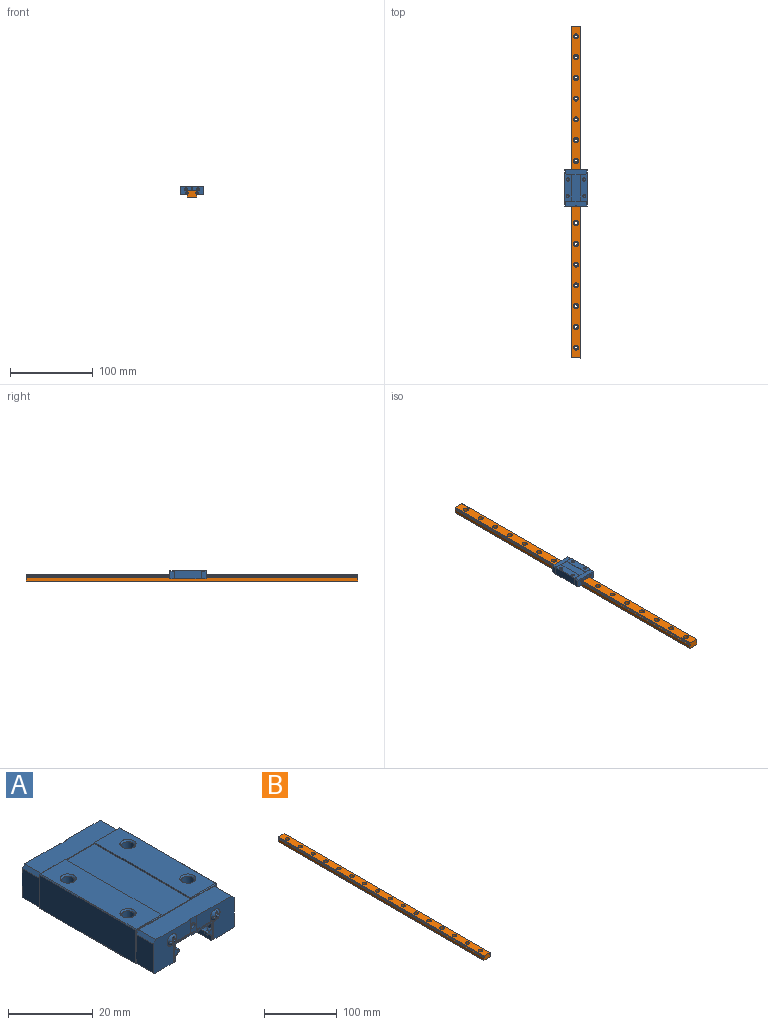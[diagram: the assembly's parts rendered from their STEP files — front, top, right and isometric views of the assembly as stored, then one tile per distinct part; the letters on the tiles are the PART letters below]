
ASSEMBLY  parts=2 mates=1
PART A: 286 faces, bbox 27.1x45.4x10.1 mm
  f0: plane 8.2x0.93mm, normal (0,-1,0), area 1.9mm2, adj f37,f39,f44,f244,f267
  f1: plane 8.2x0.93mm, normal (0,1,0), area 1.9mm2, adj f68,f70,f72,f141,f163
  f2: plane 3x3mm, normal (0,0,1), area 7.1mm2, adj f4
  f3: plane 3x3mm, normal (0,0,1), area 7.1mm2, adj f5
  f4: cylinder r=1.5mm len=5.45mm, axis (0,0,1), area 51.4mm2, adj f2,f31
  f5: cylinder r=1.5mm len=5.45mm, axis (0,0,1), area 51.4mm2, adj f3,f40
  f6: plane 8.2x0.93mm, normal (0,-1,0), area 1.9mm2, adj f26,f30,f33,f244,f266
  f7: plane 1.37x0.22mm, normal (0.71,-0.71,0), area 0.3mm2, adj f8,f50,f51,f186
  f8: cone r=1mm half-angle=45deg, axis (0,-1,0), area 1.1mm2, adj f7,f9,f10,f186
  f9: cylinder r=1mm len=32mm, axis (0,1,0), area 120.6mm2, adj f8,f11,f51,f59
  f10: plane 1.77x0.22mm, normal (0.71,-0.71,0), area 0.4mm2, adj f8,f11,f12,f186
  f11: plane 32x1.55mm, normal (1,0,0), area 49.6mm2, adj f9,f10,f13,f60
  f12: plane 12.4x0.2mm, normal (0,-0.71,-0.71), area 3.5mm2, adj f10,f13,f14,f186
  f13: plane 32x12mm, normal (0,0,-1), area 384mm2, adj f11,f12,f15,f61
  f14: plane 1.77x0.22mm, normal (-0.71,-0.71,0), area 0.4mm2, adj f12,f15,f16,f186
  f15: plane 32x1.55mm, normal (-1,0,0), area 49.6mm2, adj f13,f14,f17,f62
  f16: cone r=1.2mm half-angle=45deg, axis (0,-1,0), area 1.1mm2, adj f14,f17,f18,f186
  f17: cylinder r=1mm len=32mm, axis (0,1,0), area 120.6mm2, adj f15,f16,f19,f63
  f18: plane 1.37x0.22mm, normal (-0.71,-0.71,0), area 0.3mm2, adj f16,f19,f20,f186
  f19: plane 32x1.35mm, normal (-1,0,0), area 43.2mm2, adj f17,f18,f21,f64
  f20: plane 0.2x0.2mm, normal (-0.58,-0.58,-0.58), area 0mm2, adj f18,f21,f22
  f21: plane 32x0.2mm, normal (-0.71,0,-0.71), area 9.1mm2, adj f19,f20,f23,f65
  f22: plane 7.1x0.2mm, normal (0,-0.71,-0.71), area 2mm2, adj f20,f23,f24,f186
  f23: plane 32x7.1mm, normal (0,0,-1), area 227.2mm2, adj f21,f22,f25,f66
  f24: plane 0.2x0.2mm, normal (0.58,-0.58,-0.58), area 0mm2, adj f22,f25,f26
  f25: plane 32x0.2mm, normal (0.71,0,-0.71), area 9.1mm2, adj f23,f24,f27,f67
  f26: plane 9.6x0.2mm, normal (0.71,-0.71,0), area 2.7mm2, adj f6,f24,f27,f28,f185
  f27: plane 32x9.6mm, normal (1,0,0), area 307.2mm2, adj f25,f26,f29,f68
  f28: plane 0.2x0.2mm, normal (0.58,-0.58,0.58), area 0mm2, adj f26,f29,f30
  f29: plane 32x0.2mm, normal (0.71,0,0.71), area 9.1mm2, adj f27,f28,f32,f69
  f30: plane 8.4x0.2mm, normal (0,-0.71,0.71), area 2.3mm2, adj f6,f28,f32,f33
  f31: cone r=1.5mm half-angle=45deg, axis (0,0,1), area 6mm2, adj f4,f32
  f32: plane 32x8.4mm, normal (0,0,1), area 246.1mm2, adj f29,f30,f31,f34,f70,f71
  f33: plane 0.6x0.2mm, normal (-0.71,-0.71,0), area 0.1mm2, adj f6,f30,f34,f35,f184
  f34: plane 32x0.4mm, normal (-1,0,0), area 12.8mm2, adj f32,f33,f36,f72
  f35: plane 10.2x0.2mm, normal (0,-0.71,0.71), area 2.8mm2, adj f33,f36,f37,f184
  f36: plane 32x9.8mm, normal (0,0,1), area 313.6mm2, adj f34,f35,f38,f73
  f37: plane 0.6x0.2mm, normal (0.71,-0.71,0), area 0.1mm2, adj f0,f35,f38,f39,f184
  f38: plane 32x0.4mm, normal (1,0,0), area 12.8mm2, adj f36,f37,f41,f74
  f39: plane 8.4x0.2mm, normal (0,-0.71,0.71), area 2.3mm2, adj f0,f37,f41,f42
  f40: cone r=1.5mm half-angle=45deg, axis (0,0,1), area 6mm2, adj f5,f41
  f41: plane 32x8.4mm, normal (0,0,1), area 246.1mm2, adj f38,f39,f40,f43,f75,f76
  f42: plane 0.2x0.2mm, normal (-0.58,-0.58,0.58), area 0mm2, adj f39,f43,f44
  f43: plane 32x0.2mm, normal (-0.71,0,0.71), area 9.1mm2, adj f41,f42,f45,f77
  f44: plane 9.6x0.2mm, normal (-0.71,-0.71,0), area 2.7mm2, adj f0,f42,f45,f46,f187
  f45: plane 32x9.6mm, normal (-1,0,0), area 307.2mm2, adj f43,f44,f47,f78
  f46: plane 0.2x0.2mm, normal (-0.58,-0.58,-0.58), area 0mm2, adj f44,f47,f48
  f47: plane 32x0.2mm, normal (-0.71,0,-0.71), area 9.1mm2, adj f45,f46,f49,f79
  f48: plane 7.1x0.2mm, normal (0,-0.71,-0.71), area 2mm2, adj f46,f49,f50,f186
  f49: plane 32x7.1mm, normal (0,0,-1), area 227.2mm2, adj f47,f48,f52,f80
  f50: plane 0.2x0.2mm, normal (0.58,-0.58,-0.58), area 0mm2, adj f7,f48,f52
  f51: plane 32x1.35mm, normal (1,0,0), area 43.2mm2, adj f7,f9,f52,f58
  f52: plane 32x0.2mm, normal (0.71,0,-0.71), area 9.1mm2, adj f49,f50,f51,f81
  f53: plane 3x3mm, normal (0,0,1), area 7.1mm2, adj f55
  f54: plane 3x3mm, normal (0,0,1), area 7.1mm2, adj f56
  f55: cylinder r=1.5mm len=5.45mm, axis (0,0,1), area 51.4mm2, adj f53,f71
  f56: cylinder r=1.5mm len=5.45mm, axis (0,0,1), area 51.4mm2, adj f54,f76
  f57: plane 8.2x0.93mm, normal (0,1,0), area 1.9mm2, adj f74,f75,f78,f141,f164
  f58: plane 1.37x0.22mm, normal (0.71,0.71,0), area 0.3mm2, adj f51,f59,f81,f84
  f59: cone r=1mm half-angle=45deg, axis (0,1,0), area 1.1mm2, adj f9,f58,f60,f84
  f60: plane 1.77x0.22mm, normal (0.71,0.71,0), area 0.4mm2, adj f11,f59,f61,f84
  f61: plane 12.4x0.2mm, normal (0,0.71,-0.71), area 3.5mm2, adj f13,f60,f62,f84
  f62: plane 1.77x0.22mm, normal (-0.71,0.71,0), area 0.4mm2, adj f15,f61,f63,f84
  f63: cone r=1.2mm half-angle=45deg, axis (0,1,0), area 1.1mm2, adj f17,f62,f64,f84
  f64: plane 1.37x0.22mm, normal (-0.71,0.71,0), area 0.3mm2, adj f19,f63,f65,f84
  f65: plane 0.2x0.2mm, normal (-0.58,0.58,-0.58), area 0mm2, adj f21,f64,f66
  f66: plane 7.1x0.2mm, normal (0,0.71,-0.71), area 2mm2, adj f23,f65,f67,f84
  f67: plane 0.2x0.2mm, normal (0.58,0.58,-0.58), area 0mm2, adj f25,f66,f68
  f68: plane 9.6x0.2mm, normal (0.71,0.71,0), area 2.7mm2, adj f1,f27,f67,f69,f182
  f69: plane 0.2x0.2mm, normal (0.58,0.58,0.58), area 0mm2, adj f29,f68,f70
  f70: plane 8.4x0.2mm, normal (0,0.71,0.71), area 2.3mm2, adj f1,f32,f69,f72
  f71: cone r=1.5mm half-angle=45deg, axis (0,0,1), area 6mm2, adj f32,f55
  f72: plane 0.6x0.2mm, normal (-0.71,0.71,0), area 0.1mm2, adj f1,f34,f70,f73,f82
  f73: plane 10.2x0.2mm, normal (0,0.71,0.71), area 2.8mm2, adj f36,f72,f74,f82
  f74: plane 0.6x0.2mm, normal (0.71,0.71,0), area 0.1mm2, adj f38,f57,f73,f75,f82
  f75: plane 8.4x0.2mm, normal (0,0.71,0.71), area 2.3mm2, adj f41,f57,f74,f77
  f76: cone r=1.5mm half-angle=45deg, axis (0,0,1), area 6mm2, adj f41,f56
  f77: plane 0.2x0.2mm, normal (-0.58,0.58,0.58), area 0mm2, adj f43,f75,f78
  f78: plane 9.6x0.2mm, normal (-0.71,0.71,0), area 2.7mm2, adj f45,f57,f77,f79,f83
  f79: plane 0.2x0.2mm, normal (-0.58,0.58,-0.58), area 0mm2, adj f47,f78,f80
  f80: plane 7.1x0.2mm, normal (0,0.71,-0.71), area 2mm2, adj f49,f79,f81,f84
  f81: plane 0.2x0.2mm, normal (0.58,0.58,-0.58), area 0mm2, adj f52,f58,f80
  f82: plane 10.2x0.2mm, normal (0,-1,0), area 2mm2, adj f72,f73,f74,f141
  f83: plane 8.67x0.2mm, normal (0,-1,0), area 1.7mm2, adj f78,f146,f164,f165
  f84: plane 26.6x5.2mm, normal (0,-1,0), area 8mm2, adj f58,f59,f60,f61,f62,f63,f64,f66
  f85: sphere r=1.65mm, area 14.5mm2, adj f86,f87,f90,f92,f93,f96,f98,f99
  f86: plane 0.66x0.4mm, normal (0,0,-1), area 0.2mm2, adj f85,f87,f89,f90
  f87: plane 0.77x0.69mm, normal (-1,0,0), area 0.4mm2, adj f85,f86,f88,f108
  f88: plane 1.08x0.89mm, normal (-0.95,0.33,0), area 0.7mm2, adj f87,f89,f91,f109
  f89: plane 0.89x0.61mm, normal (0,0.33,-0.95), area 0.3mm2, adj f86,f88,f91
  f90: plane 0.77x0.69mm, normal (1,0,0), area 0.4mm2, adj f85,f86,f91,f96
  f91: plane 1.08x0.89mm, normal (0.95,0.33,0), area 0.7mm2, adj f88,f89,f90,f97
  f92: plane 0.61x0.35mm, normal (1,0,0), area 0.2mm2, adj f85,f93,f94,f96
  f93: plane 0.8x0.73mm, normal (0,0,1), area 0.4mm2, adj f85,f92,f95,f102
  f94: plane 0.89x0.61mm, normal (0.95,0.33,0), area 0.3mm2, adj f92,f95,f97
  f95: plane 1.08x0.89mm, normal (0,0.33,0.95), area 0.7mm2, adj f93,f94,f97,f103
  f96: plane 0.8x0.73mm, normal (0,0,-1), area 0.4mm2, adj f85,f90,f92,f97
  f97: plane 1.08x0.89mm, normal (0,0.33,-0.95), area 0.7mm2, adj f91,f94,f95,f96
  f98: plane 0.66x0.4mm, normal (0,0,1), area 0.2mm2, adj f85,f99,f100,f102
  f99: plane 0.77x0.69mm, normal (-1,0,0), area 0.4mm2, adj f85,f98,f101,f105
  f100: plane 0.89x0.61mm, normal (0,0.33,0.95), area 0.3mm2, adj f98,f101,f103
  f101: plane 1.08x0.89mm, normal (-0.95,0.33,0), area 0.7mm2, adj f99,f100,f103,f106
  f102: plane 0.77x0.69mm, normal (1,0,0), area 0.4mm2, adj f85,f93,f98,f103
  f103: plane 1.08x0.89mm, normal (0.95,0.33,0), area 0.7mm2, adj f95,f100,f101,f102
  f104: plane 0.61x0.35mm, normal (-1,0,0), area 0.2mm2, adj f85,f105,f107,f108
  f105: plane 0.8x0.73mm, normal (0,0,1), area 0.4mm2, adj f85,f99,f104,f106
  f106: plane 1.08x0.89mm, normal (0,0.33,0.95), area 0.7mm2, adj f101,f105,f107,f109
  f107: plane 0.89x0.61mm, normal (-0.95,0.33,0), area 0.3mm2, adj f104,f106,f109
  f108: plane 0.8x0.73mm, normal (0,0,-1), area 0.4mm2, adj f85,f87,f104,f109
  f109: plane 1.08x0.89mm, normal (0,0.33,-0.95), area 0.7mm2, adj f88,f106,f107,f108
  f110: sphere r=1.65mm, area 14.5mm2, adj f111,f112,f113,f117,f118,f120,f123,f124
  f111: plane 0.61x0.35mm, normal (-1,0,0), area 0.2mm2, adj f110,f112,f113,f114
  f112: plane 0.8x0.73mm, normal (0,0,-1), area 0.4mm2, adj f110,f111,f115,f125
  f113: plane 0.8x0.73mm, normal (0,0,1), area 0.4mm2, adj f110,f111,f116,f120
  f114: plane 0.89x0.61mm, normal (-0.95,0.33,0), area 0.3mm2, adj f111,f115,f116
  f115: plane 1.08x0.89mm, normal (0,0.33,-0.95), area 0.7mm2, adj f112,f114,f116,f128
  f116: plane 1.08x0.89mm, normal (0,0.33,0.95), area 0.7mm2, adj f113,f114,f115,f122
  f117: plane 0.66x0.4mm, normal (0,0,1), area 0.2mm2, adj f110,f118,f119,f120
  f118: plane 0.77x0.69mm, normal (1,0,0), area 0.4mm2, adj f110,f117,f121,f132
  f119: plane 0.89x0.61mm, normal (0,0.33,0.95), area 0.3mm2, adj f117,f121,f122
  f120: plane 0.77x0.69mm, normal (-1,0,0), area 0.4mm2, adj f110,f113,f117,f122
  f121: plane 1.08x0.89mm, normal (0.95,0.33,0), area 0.7mm2, adj f118,f119,f122,f134
  f122: plane 1.08x0.89mm, normal (-0.95,0.33,0), area 0.7mm2, adj f116,f119,f120,f121
  f123: plane 0.66x0.4mm, normal (0,0,-1), area 0.2mm2, adj f110,f124,f125,f126
  f124: plane 0.77x0.69mm, normal (1,0,0), area 0.4mm2, adj f110,f123,f127,f130
  f125: plane 0.77x0.69mm, normal (-1,0,0), area 0.4mm2, adj f110,f112,f123,f128
  f126: plane 0.89x0.61mm, normal (0,0.33,-0.95), area 0.3mm2, adj f123,f127,f128
  f127: plane 1.08x0.89mm, normal (0.95,0.33,0), area 0.7mm2, adj f124,f126,f128,f133
  f128: plane 1.08x0.89mm, normal (-0.95,0.33,0), area 0.7mm2, adj f115,f125,f126,f127
  f129: plane 0.61x0.35mm, normal (1,0,0), area 0.2mm2, adj f110,f130,f131,f132
  f130: plane 0.8x0.73mm, normal (0,0,-1), area 0.4mm2, adj f110,f124,f129,f133
  f131: plane 0.89x0.61mm, normal (0.95,0.33,0), area 0.3mm2, adj f129,f133,f134
  f132: plane 0.8x0.73mm, normal (0,0,1), area 0.4mm2, adj f110,f118,f129,f134
  f133: plane 1.08x0.89mm, normal (0,0.33,-0.95), area 0.7mm2, adj f127,f130,f131,f134
  f134: plane 1.08x0.89mm, normal (0,0.33,0.95), area 0.7mm2, adj f121,f131,f132,f133
  f135: plane 2.67x2mm, normal (0,-1,0), area 3.5mm2, adj f156,f157,f158,f159,f160,f180
  f136: plane 2.67x2mm, normal (0,-1,0), area 3.5mm2, adj f148,f149,f150,f151,f152,f181
  f137: plane 12.41x9.6mm, normal (0,1,0), area 77.5mm2, adj f139,f141,f142,f146,f164,f165,f169,f170
  f138: plane 12.41x9.6mm, normal (0,1,0), area 77.5mm2, adj f140,f141,f143,f162,f163,f166,f172,f173
  f139: plane 7.1x5.7mm, normal (0,0,-1), area 40.4mm2, adj f84,f137,f145,f147,f165,f167,f169,f177
  f140: plane 7.1x5.7mm, normal (0,0,-1), area 40.4mm2, adj f84,f138,f145,f161,f166,f174,f175,f178
  f141: plane 25.14x5.7mm, normal (0,0,1), area 142.9mm2, adj f1,f57,f82,f137,f138,f163,f164,f168
  f142: cylinder r=1.65mm len=3.3mm, axis (0,-1,0), area 9.1mm2, adj f110,f137,f167,f168,f169,f170
  f143: cylinder r=1.65mm len=3.3mm, axis (0,-1,0), area 9.1mm2, adj f85,f138,f168,f173,f174,f178
  f144: cylinder r=0.75mm len=1.5mm, axis (0,-1,0), area 3.3mm2, adj f168,f179
  f145: plane 12.8x5.36mm, normal (0,1,0), area 11.3mm2, adj f139,f140,f147,f148,f149,f150,f151,f152
  f146: plane 8.27x5.7mm, normal (-1,0,0), area 47.1mm2, adj f83,f137,f164,f165
  f147: plane 5.7x1.55mm, normal (1,0,0), area 8.8mm2, adj f84,f139,f145,f148,f181
  f148: cylinder r=1mm len=0.9mm, axis (0,-1,0), area 0.9mm2, adj f136,f145,f147,f149
  f149: plane 0.9x0.71mm, normal (0,0,-1), area 0.6mm2, adj f136,f145,f148,f150
  f150: plane 0.9x0.6mm, normal (1,0,0), area 0.5mm2, adj f136,f145,f149,f151
  f151: plane 0.9x0.71mm, normal (0,0,1), area 0.6mm2, adj f136,f145,f150,f152
  f152: cylinder r=1mm len=0.9mm, axis (0,-1,0), area 0.9mm2, adj f136,f145,f151,f153
  f153: plane 5.7x1.55mm, normal (1,0,0), area 8.8mm2, adj f84,f145,f152,f154,f181
  f154: plane 12x5.7mm, normal (0,0,-1), area 68.4mm2, adj f84,f145,f153,f155
  f155: plane 5.7x1.55mm, normal (-1,0,0), area 8.8mm2, adj f84,f145,f154,f156,f180
  f156: cylinder r=1mm len=0.9mm, axis (0,-1,0), area 0.9mm2, adj f135,f145,f155,f157
  f157: plane 0.9x0.71mm, normal (0,0,1), area 0.6mm2, adj f135,f145,f156,f158
  f158: plane 0.9x0.6mm, normal (-1,0,0), area 0.5mm2, adj f135,f145,f157,f159
  f159: plane 0.9x0.71mm, normal (0,0,-1), area 0.6mm2, adj f135,f145,f158,f160
  f160: cylinder r=1mm len=0.9mm, axis (0,-1,0), area 0.9mm2, adj f135,f145,f159,f161
  f161: plane 5.7x1.55mm, normal (-1,0,0), area 8.8mm2, adj f84,f140,f145,f160,f180
  f162: plane 8.27x5.7mm, normal (1,0,0), area 47.1mm2, adj f138,f163,f166,f182
  f163: plane 5.7x0.93mm, normal (0.71,0,0.71), area 7.5mm2, adj f1,f138,f141,f162,f182
  f164: plane 5.7x0.93mm, normal (-0.71,0,0.71), area 7.5mm2, adj f57,f83,f137,f141,f146
  f165: plane 5.7x0.4mm, normal (-0.71,0,-0.71), area 3.2mm2, adj f83,f84,f137,f139,f146
  f166: plane 5.7x0.4mm, normal (0.71,0,-0.71), area 3.2mm2, adj f84,f138,f140,f162,f182
  f167: plane 5.36x0.4mm, normal (0,1,0), area 2.1mm2, adj f139,f142,f169,f177
  f168: plane 12.8x4.24mm, normal (0,1,0), area 11.5mm2, adj f141,f142,f143,f144,f170,f171,f172,f173
  f169: plane 5.2x0.2mm, normal (1,0,0), area 1mm2, adj f137,f139,f142,f167
  f170: plane 4.83x0.2mm, normal (0,0,-1), area 1mm2, adj f137,f142,f168,f171
  f171: plane 3.84x0.2mm, normal (1,0,0), area 0.8mm2, adj f137,f141,f168,f170
  f172: plane 3.84x0.2mm, normal (-1,0,0), area 0.8mm2, adj f138,f141,f168,f173
  f173: plane 4.83x0.2mm, normal (0,0,-1), area 1mm2, adj f138,f143,f168,f172
  f174: plane 5.2x0.2mm, normal (-1,0,0), area 1mm2, adj f138,f140,f143,f178
  f175: plane 5.36x0.2mm, normal (1,0,0), area 1.1mm2, adj f140,f145,f176,f178
  f176: plane 12.8x0.2mm, normal (0,0,1), area 2.6mm2, adj f145,f168,f175,f177
  f177: plane 5.36x0.2mm, normal (-1,0,0), area 1.1mm2, adj f139,f145,f167,f176
  f178: plane 5.36x0.4mm, normal (0,1,0), area 2.1mm2, adj f140,f143,f174,f175
  f179: cylinder r=0.75mm len=4.8mm, axis (0,-1,0), area 22.6mm2, adj f144,f183
  f180: cylinder r=1mm len=4.8mm, axis (0,-1,0), area 18.1mm2, adj f84,f135,f155,f161
  f181: cylinder r=1mm len=4.8mm, axis (0,-1,0), area 18.1mm2, adj f84,f136,f147,f153
  f182: plane 8.67x0.2mm, normal (0,-1,0), area 1.7mm2, adj f68,f162,f163,f166
  f183: plane 1.5x1.5mm, normal (0,1,0), area 1.8mm2, adj f179
  f184: plane 10.2x0.2mm, normal (0,1,0), area 2mm2, adj f33,f35,f37,f244
  f185: plane 8.67x0.2mm, normal (0,1,0), area 1.7mm2, adj f26,f265,f266,f269
  f186: plane 26.6x5.2mm, normal (0,1,0), area 8mm2, adj f7,f8,f10,f12,f14,f16,f18,f22
  f187: plane 8.67x0.2mm, normal (0,1,0), area 1.7mm2, adj f44,f249,f267,f268
  f188: sphere r=1.65mm, area 14.5mm2, adj f189,f190,f193,f195,f196,f199,f201,f202
  f189: plane 0.66x0.4mm, normal (0,0,-1), area 0.2mm2, adj f188,f190,f192,f193
  f190: plane 0.77x0.69mm, normal (-1,0,0), area 0.4mm2, adj f188,f189,f191,f211
  f191: plane 1.08x0.89mm, normal (-0.95,-0.33,0), area 0.7mm2, adj f190,f192,f194,f212
  f192: plane 0.89x0.61mm, normal (0,-0.33,-0.95), area 0.3mm2, adj f189,f191,f194
  f193: plane 0.77x0.69mm, normal (1,0,0), area 0.4mm2, adj f188,f189,f194,f199
  f194: plane 1.08x0.89mm, normal (0.95,-0.33,0), area 0.7mm2, adj f191,f192,f193,f200
  f195: plane 0.61x0.35mm, normal (1,0,0), area 0.2mm2, adj f188,f196,f197,f199
  f196: plane 0.8x0.73mm, normal (0,0,1), area 0.4mm2, adj f188,f195,f198,f205
  f197: plane 0.89x0.61mm, normal (0.95,-0.33,0), area 0.3mm2, adj f195,f198,f200
  f198: plane 1.08x0.89mm, normal (0,-0.33,0.95), area 0.7mm2, adj f196,f197,f200,f206
  f199: plane 0.8x0.73mm, normal (0,0,-1), area 0.4mm2, adj f188,f193,f195,f200
  f200: plane 1.08x0.89mm, normal (0,-0.33,-0.95), area 0.7mm2, adj f194,f197,f198,f199
  f201: plane 0.66x0.4mm, normal (0,0,1), area 0.2mm2, adj f188,f202,f203,f205
  f202: plane 0.77x0.69mm, normal (-1,0,0), area 0.4mm2, adj f188,f201,f204,f208
  f203: plane 0.89x0.61mm, normal (0,-0.33,0.95), area 0.3mm2, adj f201,f204,f206
  f204: plane 1.08x0.89mm, normal (-0.95,-0.33,0), area 0.7mm2, adj f202,f203,f206,f209
  f205: plane 0.77x0.69mm, normal (1,0,0), area 0.4mm2, adj f188,f196,f201,f206
  f206: plane 1.08x0.89mm, normal (0.95,-0.33,0), area 0.7mm2, adj f198,f203,f204,f205
  f207: plane 0.61x0.35mm, normal (-1,0,0), area 0.2mm2, adj f188,f208,f210,f211
  f208: plane 0.8x0.73mm, normal (0,0,1), area 0.4mm2, adj f188,f202,f207,f209
  f209: plane 1.08x0.89mm, normal (0,-0.33,0.95), area 0.7mm2, adj f204,f208,f210,f212
  f210: plane 0.89x0.61mm, normal (-0.95,-0.33,0), area 0.3mm2, adj f207,f209,f212
  f211: plane 0.8x0.73mm, normal (0,0,-1), area 0.4mm2, adj f188,f190,f207,f212
  f212: plane 1.08x0.89mm, normal (0,-0.33,-0.95), area 0.7mm2, adj f191,f209,f210,f211
  f213: sphere r=1.65mm, area 14.5mm2, adj f214,f215,f216,f220,f221,f223,f226,f227
  f214: plane 0.61x0.35mm, normal (-1,0,0), area 0.2mm2, adj f213,f215,f216,f217
  f215: plane 0.8x0.73mm, normal (0,0,-1), area 0.4mm2, adj f213,f214,f218,f228
  f216: plane 0.8x0.73mm, normal (0,0,1), area 0.4mm2, adj f213,f214,f219,f223
  f217: plane 0.89x0.61mm, normal (-0.95,-0.33,0), area 0.3mm2, adj f214,f218,f219
  f218: plane 1.08x0.89mm, normal (0,-0.33,-0.95), area 0.7mm2, adj f215,f217,f219,f231
  f219: plane 1.08x0.89mm, normal (0,-0.33,0.95), area 0.7mm2, adj f216,f217,f218,f225
  f220: plane 0.66x0.4mm, normal (0,0,1), area 0.2mm2, adj f213,f221,f222,f223
  f221: plane 0.77x0.69mm, normal (1,0,0), area 0.4mm2, adj f213,f220,f224,f235
  f222: plane 0.89x0.61mm, normal (0,-0.33,0.95), area 0.3mm2, adj f220,f224,f225
  f223: plane 0.77x0.69mm, normal (-1,0,0), area 0.4mm2, adj f213,f216,f220,f225
  f224: plane 1.08x0.89mm, normal (0.95,-0.33,0), area 0.7mm2, adj f221,f222,f225,f237
  f225: plane 1.08x0.89mm, normal (-0.95,-0.33,0), area 0.7mm2, adj f219,f222,f223,f224
  f226: plane 0.66x0.4mm, normal (0,0,-1), area 0.2mm2, adj f213,f227,f228,f229
  f227: plane 0.77x0.69mm, normal (1,0,0), area 0.4mm2, adj f213,f226,f230,f233
  f228: plane 0.77x0.69mm, normal (-1,0,0), area 0.4mm2, adj f213,f215,f226,f231
  f229: plane 0.89x0.61mm, normal (0,-0.33,-0.95), area 0.3mm2, adj f226,f230,f231
  f230: plane 1.08x0.89mm, normal (0.95,-0.33,0), area 0.7mm2, adj f227,f229,f231,f236
  f231: plane 1.08x0.89mm, normal (-0.95,-0.33,0), area 0.7mm2, adj f218,f228,f229,f230
  f232: plane 0.61x0.35mm, normal (1,0,0), area 0.2mm2, adj f213,f233,f234,f235
  f233: plane 0.8x0.73mm, normal (0,0,-1), area 0.4mm2, adj f213,f227,f232,f236
  f234: plane 0.89x0.61mm, normal (0.95,-0.33,0), area 0.3mm2, adj f232,f236,f237
  f235: plane 0.8x0.73mm, normal (0,0,1), area 0.4mm2, adj f213,f221,f232,f237
  f236: plane 1.08x0.89mm, normal (0,-0.33,-0.95), area 0.7mm2, adj f230,f233,f234,f237
  f237: plane 1.08x0.89mm, normal (0,-0.33,0.95), area 0.7mm2, adj f224,f234,f235,f236
  f238: plane 2.67x2mm, normal (0,1,0), area 3.5mm2, adj f251,f252,f253,f254,f255,f284
  f239: plane 2.67x2mm, normal (0,1,0), area 3.5mm2, adj f259,f260,f261,f262,f263,f283
  f240: plane 12.41x9.6mm, normal (0,-1,0), area 77.5mm2, adj f242,f244,f245,f249,f267,f268,f272,f273
  f241: plane 12.41x9.6mm, normal (0,-1,0), area 77.5mm2, adj f243,f244,f246,f265,f266,f269,f275,f276
  f242: plane 7.1x5.7mm, normal (0,0,-1), area 40.4mm2, adj f186,f240,f248,f250,f268,f270,f272,f280
  f243: plane 7.1x5.7mm, normal (0,0,-1), area 40.4mm2, adj f186,f241,f248,f264,f269,f277,f278,f281
  f244: plane 25.14x5.7mm, normal (0,0,1), area 142.9mm2, adj f0,f6,f184,f240,f241,f266,f267,f271
  f245: cylinder r=1.65mm len=3.3mm, axis (0,1,0), area 9.1mm2, adj f213,f240,f270,f271,f272,f273
  f246: cylinder r=1.65mm len=3.3mm, axis (0,1,0), area 9.1mm2, adj f188,f241,f271,f276,f277,f281
  f247: cylinder r=0.75mm len=1.5mm, axis (0,1,0), area 3.3mm2, adj f271,f282
  f248: plane 12.8x5.36mm, normal (0,-1,0), area 11.3mm2, adj f242,f243,f250,f251,f252,f253,f254,f255
  f249: plane 8.27x5.7mm, normal (-1,0,0), area 47.1mm2, adj f187,f240,f267,f268
  f250: plane 5.7x1.55mm, normal (1,0,0), area 8.8mm2, adj f186,f242,f248,f251,f284
  f251: cylinder r=1mm len=0.9mm, axis (0,1,0), area 0.9mm2, adj f238,f248,f250,f252
  f252: plane 0.9x0.71mm, normal (0,0,-1), area 0.6mm2, adj f238,f248,f251,f253
  f253: plane 0.9x0.6mm, normal (1,0,0), area 0.5mm2, adj f238,f248,f252,f254
  f254: plane 0.9x0.71mm, normal (0,0,1), area 0.6mm2, adj f238,f248,f253,f255
  f255: cylinder r=1mm len=0.9mm, axis (0,1,0), area 0.9mm2, adj f238,f248,f254,f256
  f256: plane 5.7x1.55mm, normal (1,0,0), area 8.8mm2, adj f186,f248,f255,f257,f284
  f257: plane 12x5.7mm, normal (0,0,-1), area 68.4mm2, adj f186,f248,f256,f258
  f258: plane 5.7x1.55mm, normal (-1,0,0), area 8.8mm2, adj f186,f248,f257,f259,f283
  f259: cylinder r=1mm len=0.9mm, axis (0,1,0), area 0.9mm2, adj f239,f248,f258,f260
  f260: plane 0.9x0.71mm, normal (0,0,1), area 0.6mm2, adj f239,f248,f259,f261
  f261: plane 0.9x0.6mm, normal (-1,0,0), area 0.5mm2, adj f239,f248,f260,f262
  f262: plane 0.9x0.71mm, normal (0,0,-1), area 0.6mm2, adj f239,f248,f261,f263
  f263: cylinder r=1mm len=0.9mm, axis (0,1,0), area 0.9mm2, adj f239,f248,f262,f264
  f264: plane 5.7x1.55mm, normal (-1,0,0), area 8.8mm2, adj f186,f243,f248,f263,f283
  f265: plane 8.27x5.7mm, normal (1,0,0), area 47.1mm2, adj f185,f241,f266,f269
  f266: plane 5.7x0.93mm, normal (0.71,0,0.71), area 7.5mm2, adj f6,f185,f241,f244,f265
  f267: plane 5.7x0.93mm, normal (-0.71,0,0.71), area 7.5mm2, adj f0,f187,f240,f244,f249
  f268: plane 5.7x0.4mm, normal (-0.71,0,-0.71), area 3.2mm2, adj f186,f187,f240,f242,f249
  f269: plane 5.7x0.4mm, normal (0.71,0,-0.71), area 3.2mm2, adj f185,f186,f241,f243,f265
  f270: plane 5.36x0.4mm, normal (0,-1,0), area 2.1mm2, adj f242,f245,f272,f280
  f271: plane 12.8x4.24mm, normal (0,-1,0), area 11.5mm2, adj f244,f245,f246,f247,f273,f274,f275,f276
  f272: plane 5.2x0.2mm, normal (1,0,0), area 1mm2, adj f240,f242,f245,f270
  f273: plane 4.83x0.2mm, normal (0,0,-1), area 1mm2, adj f240,f245,f271,f274
  f274: plane 3.84x0.2mm, normal (1,0,0), area 0.8mm2, adj f240,f244,f271,f273
  f275: plane 3.84x0.2mm, normal (-1,0,0), area 0.8mm2, adj f241,f244,f271,f276
  f276: plane 4.83x0.2mm, normal (0,0,-1), area 1mm2, adj f241,f246,f271,f275
  f277: plane 5.2x0.2mm, normal (-1,0,0), area 1mm2, adj f241,f243,f246,f281
  f278: plane 5.36x0.2mm, normal (1,0,0), area 1.1mm2, adj f243,f248,f279,f281
  f279: plane 12.8x0.2mm, normal (0,0,1), area 2.6mm2, adj f248,f271,f278,f280
  f280: plane 5.36x0.2mm, normal (-1,0,0), area 1.1mm2, adj f242,f248,f270,f279
  f281: plane 5.36x0.4mm, normal (0,-1,0), area 2.1mm2, adj f243,f246,f277,f278
  f282: cylinder r=0.75mm len=4.8mm, axis (0,1,0), area 22.6mm2, adj f247,f285
  f283: cylinder r=1mm len=4.8mm, axis (0,1,0), area 18.1mm2, adj f186,f239,f258,f264
  f284: cylinder r=1mm len=4.8mm, axis (0,1,0), area 18.1mm2, adj f186,f238,f250,f256
  f285: plane 1.5x1.5mm, normal (0,-1,0), area 1.8mm2, adj f282
PART B: 70 faces, bbox 12x400x8 mm
  f0: plane 400x1.25mm, normal (-1,0,0), area 499.6mm2, adj f1,f19,f20,f51
  f1: cylinder r=1mm len=400mm, axis (0,1,0), area 381.5mm2, adj f0,f2,f20,f51
  f2: plane 400x0.71mm, normal (0,0,-1), area 284.4mm2, adj f1,f3,f20,f51
  f3: plane 400x0.6mm, normal (-1,0,0), area 238.4mm2, adj f2,f4,f20,f51
  f4: plane 400x0.71mm, normal (0,0,1), area 284.4mm2, adj f3,f5,f20,f51
  f5: cylinder r=1mm len=400mm, axis (0,1,0), area 381.5mm2, adj f4,f6,f20,f51
  f6: plane 400x4.25mm, normal (-1,0,0), area 1699.6mm2, adj f5,f7,f20,f51
  f7: plane 400x0.3mm, normal (-0.71,0,-0.71), area 169.7mm2, adj f6,f8,f20,f51
  f8: plane 400x11.4mm, normal (0,0,-1), area 4406.1mm2, adj f7,f9,f20,f23,f42,f43,f44,f45
  f9: plane 400x0.3mm, normal (0.71,0,-0.71), area 169.7mm2, adj f8,f10,f20,f51
  f10: plane 400x4.25mm, normal (1,0,0), area 1699.6mm2, adj f9,f11,f20,f51
  f11: cylinder r=1mm len=400mm, axis (0,1,0), area 381.5mm2, adj f10,f12,f20,f51
  f12: plane 400x0.71mm, normal (0,0,1), area 284.4mm2, adj f11,f13,f20,f51
  f13: plane 400x0.6mm, normal (1,0,0), area 238.4mm2, adj f12,f14,f20,f51
  f14: plane 400x0.71mm, normal (0,0,-1), area 284.4mm2, adj f13,f15,f20,f51
  f15: cylinder r=1mm len=400mm, axis (0,1,0), area 381.5mm2, adj f14,f16,f20,f51
  f16: plane 400x1.25mm, normal (1,0,0), area 499.6mm2, adj f15,f17,f20,f51
  f17: plane 400x0.3mm, normal (0.71,0,0.71), area 169.7mm2, adj f16,f18,f20,f51
  f18: plane 400x11.4mm, normal (0,0,1), area 4107.6mm2, adj f17,f19,f20,f21,f24,f27,f29,f31
  f19: plane 400x0.3mm, normal (-0.71,0,0.71), area 169.7mm2, adj f0,f18,f20,f51
  f20: plane 12x8mm, normal (0,1,0), area 93.1mm2, adj f0,f1,f2,f3,f4,f5,f6,f7
  f21: cylinder r=3mm len=6mm, axis (0,0,1), area 84.8mm2, adj f18,f22
  f22: plane 6x6mm, normal (0,0,1), area 18.7mm2, adj f21,f23
  f23: cylinder r=1.75mm len=3.5mm, axis (0,0,1), area 38.5mm2, adj f8,f22
  f24: cylinder r=3mm len=6mm, axis (0,0,1), area 84.8mm2, adj f18,f25
  f25: plane 6x6mm, normal (0,0,1), area 18.7mm2, adj f24,f42
  f26: plane 6x6mm, normal (0,0,1), area 18.7mm2, adj f27,f43
  f27: cylinder r=3mm len=6mm, axis (0,0,1), area 84.8mm2, adj f18,f26
  f28: plane 6x6mm, normal (0,0,1), area 18.7mm2, adj f29,f44
  f29: cylinder r=3mm len=6mm, axis (0,0,1), area 84.8mm2, adj f18,f28
  f30: plane 6x6mm, normal (0,0,1), area 18.7mm2, adj f31,f45
  f31: cylinder r=3mm len=6mm, axis (0,0,1), area 84.8mm2, adj f18,f30
  f32: plane 6x6mm, normal (0,0,1), area 18.7mm2, adj f33,f46
  f33: cylinder r=3mm len=6mm, axis (0,0,1), area 84.8mm2, adj f18,f32
  f34: plane 6x6mm, normal (0,0,1), area 18.7mm2, adj f35,f47
  f35: cylinder r=3mm len=6mm, axis (0,0,1), area 84.8mm2, adj f18,f34
  f36: plane 6x6mm, normal (0,0,1), area 18.7mm2, adj f37,f48
  f37: cylinder r=3mm len=6mm, axis (0,0,1), area 84.8mm2, adj f18,f36
  f38: plane 6x6mm, normal (0,0,1), area 18.7mm2, adj f39,f49
  f39: cylinder r=3mm len=6mm, axis (0,0,1), area 84.8mm2, adj f18,f38
  f40: plane 6x6mm, normal (0,0,1), area 18.7mm2, adj f41,f50
  f41: cylinder r=3mm len=6mm, axis (0,0,1), area 84.8mm2, adj f18,f40
  f42: cylinder r=1.75mm len=3.5mm, axis (0,0,1), area 38.5mm2, adj f8,f25
  f43: cylinder r=1.75mm len=3.5mm, axis (0,0,1), area 38.5mm2, adj f8,f26
  f44: cylinder r=1.75mm len=3.5mm, axis (0,0,1), area 38.5mm2, adj f8,f28
  f45: cylinder r=1.75mm len=3.5mm, axis (0,0,1), area 38.5mm2, adj f8,f30
  f46: cylinder r=1.75mm len=3.5mm, axis (0,0,1), area 38.5mm2, adj f8,f32
  f47: cylinder r=1.75mm len=3.5mm, axis (0,0,1), area 38.5mm2, adj f8,f34
  f48: cylinder r=1.75mm len=3.5mm, axis (0,0,1), area 38.5mm2, adj f8,f36
  f49: cylinder r=1.75mm len=3.5mm, axis (0,0,1), area 38.5mm2, adj f8,f38
  f50: cylinder r=1.75mm len=3.5mm, axis (0,0,1), area 38.5mm2, adj f8,f40
  f51: plane 12x8mm, normal (0,-1,0), area 93.1mm2, adj f0,f1,f2,f3,f4,f5,f6,f7
  f52: cylinder r=3mm len=6mm, axis (0,0,1), area 75.4mm2, adj f18,f53
  f53: plane 6x6mm, normal (0,0,1), area 18.7mm2, adj f52,f69
  f54: cylinder r=3mm len=6mm, axis (0,0,1), area 75.4mm2, adj f18,f55
  f55: plane 6x6mm, normal (0,0,1), area 18.7mm2, adj f54,f68
  f56: cylinder r=3mm len=6mm, axis (0,0,1), area 75.4mm2, adj f18,f57
  f57: plane 6x6mm, normal (0,0,1), area 18.7mm2, adj f56,f67
  f58: cylinder r=3mm len=6mm, axis (0,0,1), area 75.4mm2, adj f18,f59
  f59: plane 6x6mm, normal (0,0,1), area 18.7mm2, adj f58,f66
  f60: cylinder r=3mm len=6mm, axis (0,0,1), area 75.4mm2, adj f18,f61
  f61: plane 6x6mm, normal (0,0,1), area 18.7mm2, adj f60,f65
  f62: cylinder r=3mm len=6mm, axis (0,0,1), area 75.4mm2, adj f18,f63
  f63: plane 6x6mm, normal (0,0,1), area 18.7mm2, adj f62,f64
  f64: cylinder r=1.75mm len=4mm, axis (0,0,1), area 44mm2, adj f8,f63
  f65: cylinder r=1.75mm len=4mm, axis (0,0,1), area 44mm2, adj f8,f61
  f66: cylinder r=1.75mm len=4mm, axis (0,0,1), area 44mm2, adj f8,f59
  f67: cylinder r=1.75mm len=4mm, axis (0,0,1), area 44mm2, adj f8,f57
  f68: cylinder r=1.75mm len=4mm, axis (0,0,1), area 44mm2, adj f8,f55
  f69: cylinder r=1.75mm len=4mm, axis (0,0,1), area 44mm2, adj f8,f53
PLACE A t=(-0.12,0.42,4.86)mm
PLACE B rot(axis=(0,1,0),0deg) t=(-0.12,195.41,0.86)mm fixed
MATE slider B.f51 <-> A.f271  axis (0,-1,0) through (-0.12,-204.59,0.81)mm
